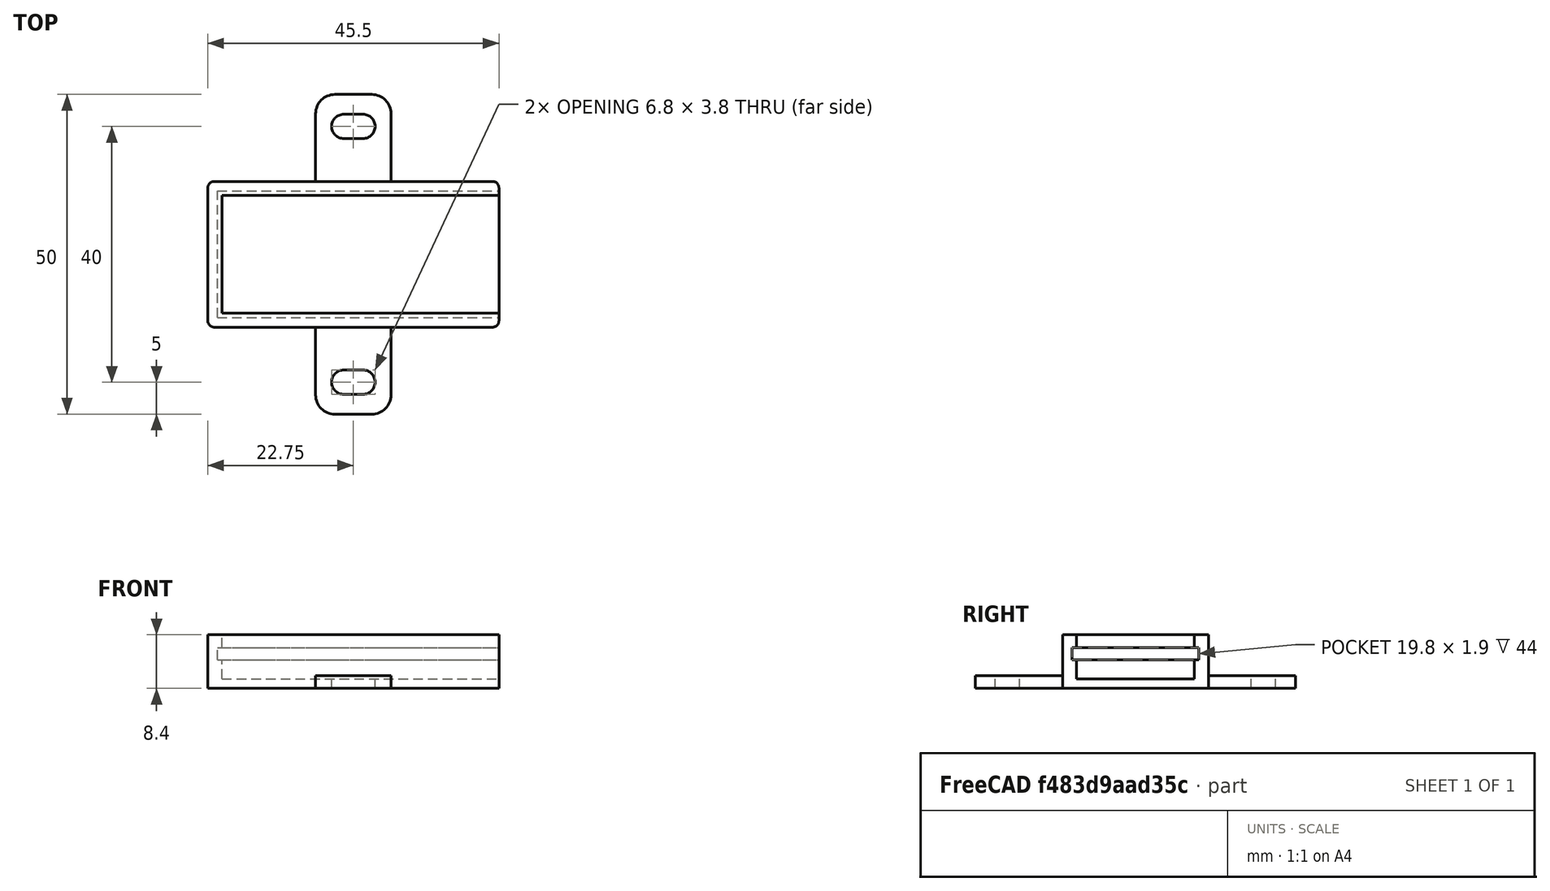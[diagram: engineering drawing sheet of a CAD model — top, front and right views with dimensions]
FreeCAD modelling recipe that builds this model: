
FCSTD DOCUMENT  (FreeCAD 0.19R)
Label: picaxe20m2_uni_pcb_1
License: FreeArt
LicenseURL: http://artlibre.org/licence/lal
objects: Part::Box×3, Part::MultiFuse×2, Spreadsheet::Sheet×1, Part::Fillet×1, Part::Feature×1, Part::Cut×1, App::Part×1
note: 8 computed .brp shape members not serialized (recipe doc carries the construction recipe); baked Part::Feature solids carry a one-line shape summary decoded from their .brp

FEATURE [Spreadsheet::Sheet] Spreadsheet  label="p"
  cells = A1=pcb_x; B1(pcb_x)=44; A2=pcb_y; B2(pcb_y)=19.8; A3=pcb_z; B3(pcb_z)=1.9; A4=pcb_under; B4(pcb_under)=3; A5=side_wall; B5(side_wall)=1.5; A6=pcb_side_lane; B6(pcb_side_lane)=0.7; A7=bottom_wall; B7(bottom_wall)=1.5; A8=pcb_above; B8(pcb_above)=2
FEATURE [Part::Box] Box  label="external cube"
  AttacherType = Attacher::AttachEngine3D
  Height = 8.4
  Length = 45.5
  Width = 22.8
  expr: Length = <<p>>.pcb_x + <<p>>.side_wall
  expr: Width = <<p>>.pcb_y + 2 * <<p>>.side_wall
  expr: Height = <<p>>.bottom_wall + <<p>>.pcb_under + <<p>>.pcb_z + <<p>>.pcb_above
FEATURE [Part::Box] Box006  label="internal cube"
  AttacherType = Attacher::AttachEngine3D
  Height = 6.9
  Length = 44.1
  Placement = pos=(2.2,2.2,1.5) rot=(0,0,1;0rad)
  Width = 18.4
  expr: Length = <<p>>.pcb_x - 2 * <<p>>.pcb_side_lane + <<p>>.side_wall
  expr: Width = <<p>>.pcb_y - 2 * <<p>>.pcb_side_lane
  expr: Height = <<p>>.pcb_under + <<p>>.pcb_z + <<p>>.pcb_above
  expr: .Placement.Base.z = <<p>>.bottom_wall
  expr: .Placement.Base.x = <<p>>.side_wall + <<p>>.pcb_side_lane
  expr: .Placement.Base.y = <<p>>.side_wall + <<p>>.pcb_side_lane
FEATURE [Part::Box] Box007  label="pcb extract cube"
  AttacherType = Attacher::AttachEngine3D
  Height = 1.9
  Length = 44
  Placement = pos=(1.5,1.5,4.5) rot=(0,0,1;0rad)
  Width = 19.8
  expr: Height = <<p>>.pcb_z
  expr: .Placement.Base.z = <<p>>.bottom_wall + <<p>>.pcb_under
  expr: Width = <<p>>.pcb_y
  expr: Length = <<p>>.pcb_x
  expr: .Placement.Base.x = <<p>>.side_wall
  expr: .Placement.Base.y = <<p>>.side_wall
FEATURE [Part::MultiFuse] Fusion  label="extract fusion"
  Shapes = -> [Box006,Box007]
FEATURE [Part::Fillet] Fillet  label="external fillet"
  Base = -> Box
  Edges = 4 edges r=1: [Edge1,Edge3,Edge5,Edge7]
FEATURE [Part::Feature] Cut002002  label="attach plane y dir002"
  Placement = pos=(16.85,-13.6,0) rot=(0,0,1;0rad)
  shape: bbox 11.8 x 50 x 2 mm, 20 faces (baked)
FEATURE [Part::MultiFuse] Fusion001  label="solid fusion"
  Shapes = -> [Fillet,Cut002002]
FEATURE [Part::Cut] Cut  label="body cut"
  Base = -> Fusion001
  Tool = -> Fusion
FEATURE [App::Part] Part  label="picaxe20m2 pcb box part"
  Group = -> [Box,Fillet,Fusion001,Fusion,Box007,Box006,Cut]
  Origin = -> Origin
